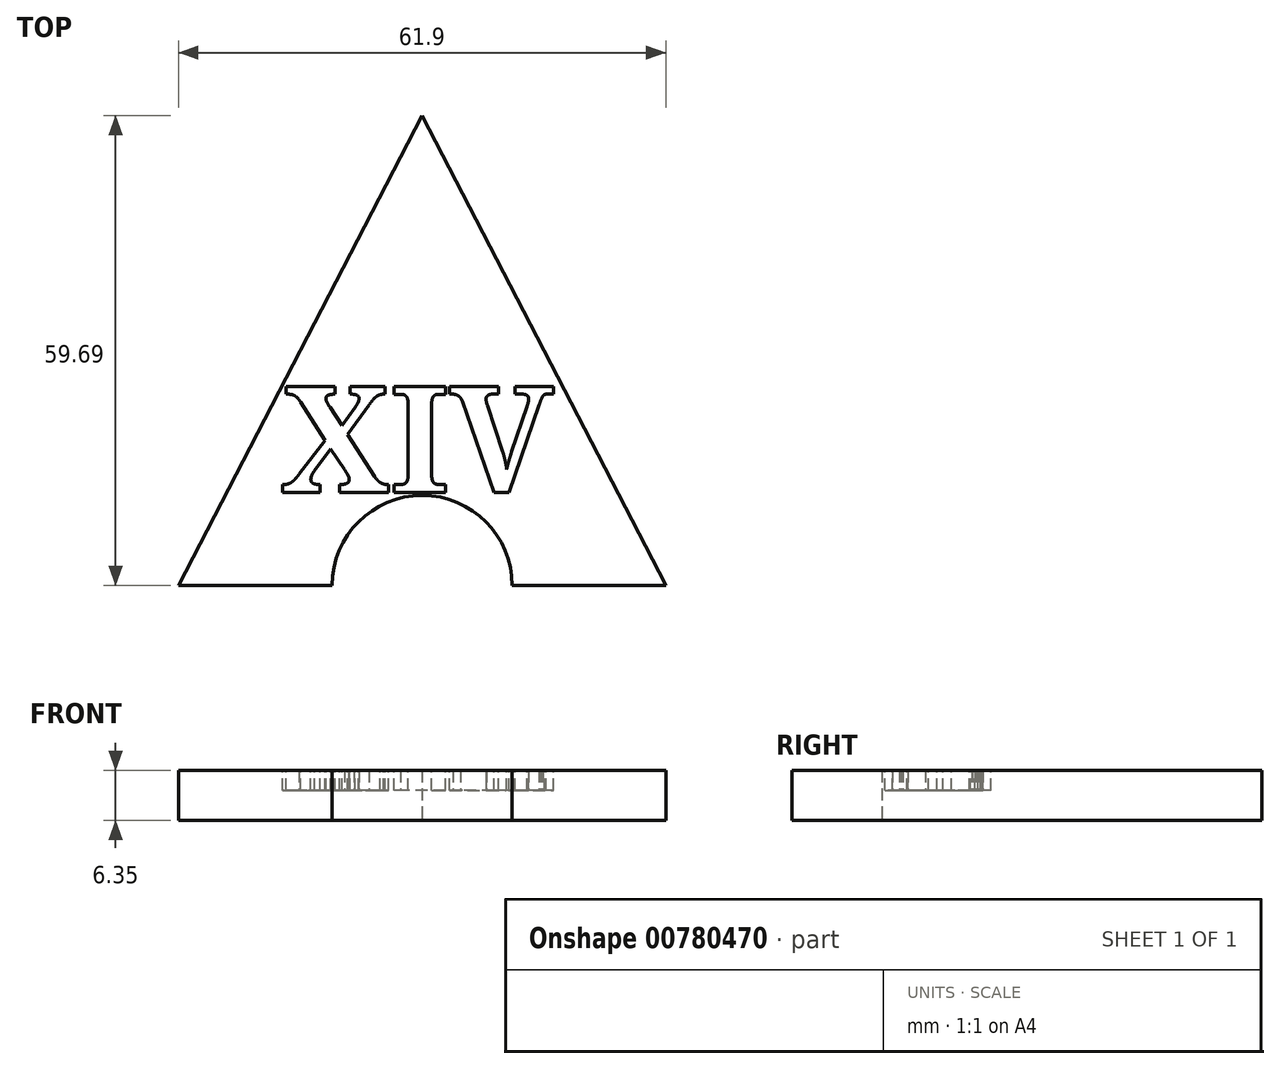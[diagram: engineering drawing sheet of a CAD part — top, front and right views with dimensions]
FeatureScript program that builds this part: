
annotation { "Feature Type Name" : "Feature", "Feature Type Description" : "" }
export const myFeature = defineFeature(function(context is Context, id is Id, definition is map)
    precondition{}
    {
        {
            var Q0;
            Q0=qCreatedBy(makeId("Top.planeOp"),FACE);
            var sketch = newSketch(context, id + "F0", { "sketchPlane" : qUnion([Q0])});
            skCircle(sketch, "E0.cCircle", {"center": v(0, 1.69) * mm, "radius": 17.87 * mm, "construction": true});
            skLineSegment(sketch, "E0.0", {"start": v(30.95, -16.18) * mm, "end": v(-30.95, -16.18) * mm});
            skLineSegment(sketch, "E0.1", {"start": v(-30.95, -16.18) * mm, "end": v(0, 43.5) * mm});
            skLineSegment(sketch, "E0.2", {"start": v(0, 43.5) * mm, "end": v(30.95, -16.18) * mm});
            skPoint(sketch, "E0.0.midPoint", {"position": v(0, -16.18) * mm});
            skSolve(sketch);
        }
        {
            var Q0;
            Q0=makeQuery(id+"F0.imprint","IMPRINT",FACE,{"disambiguationData":[TD([[makeQuery(id+"F0.imprint","IMPRINT",EDGE,{"derivedFrom":sQuery(id+"F0.wireOp",EDGE,"E0.0")}),-1.0]])]});
            extrude(context, id + "F1", {"entities" : qUnion([Q0]), "depth" : 6.35 * mm, "offsetDistance" : 25.4 * mm});
        }
        {
            var Q0;
            Q0=sQuery(id+"F0.wireOp",VERTEX,"E0.0.midPoint");
            var Q1;
            Q1=makeQuery(id+"F1.opExtrude","SWEPT_BODY",BODY,{"disambiguationData":[OSD([sQuery(id+"F0.wireOp",EDGE,"E0.0"),sQuery(id+"F0.wireOp",EDGE,"E0.1"),sQuery(id+"F0.wireOp",EDGE,"E0.2")])]});
            hole(context, id + "F2", {"style" : HoleStyle.SIMPLE, "endStyle" : HoleEndStyle.THROUGH, "oppositeDirection" : true, "holeDiameter" : 22.86 * mm, "majorDiameter" : 6.35 * mm, "isTappedThrough" : true, "tappedDepth" : 12.7 * mm, "tapClearance" : 3, "locations" : qUnion([Q0]), "scope" : qUnion([Q1])});
        }
        {
            var Q0;
            Q0=makeQuery(id+"F1.opExtrude","CAP_FACE",FACE,{"disambiguationData":[OSD([sQuery(id+"F0.wireOp",EDGE,"E0.0"),sQuery(id+"F0.wireOp",EDGE,"E0.1"),sQuery(id+"F0.wireOp",EDGE,"E0.2")])],"isStart":false});
            var sketch = newSketch(context, id + "F3", { "sketchPlane" : qUnion([Q0])});
            skText(sketch, "E1", { "text": "XIV", "fontName": "NotoSerif-Bold.ttf"});
            const initialGuessF3  = {"E1": [-0.01789, -0.00437, 1, 0, 0.01359]};
            skSetInitialGuess(sketch, initialGuessF3);
            skSolve(sketch);
        }
        {
            var Q0;
            Q0 = qSketchRegion(id + "F3", true);
            extrude(context, id + "F4", {"entities" : qUnion([Q0]), "operationType" : NewBodyOperationType.REMOVE, "oppositeDirection" : true, "depth" : 2.54 * mm, "offsetDistance" : 25.4 * mm});
        }
    });
